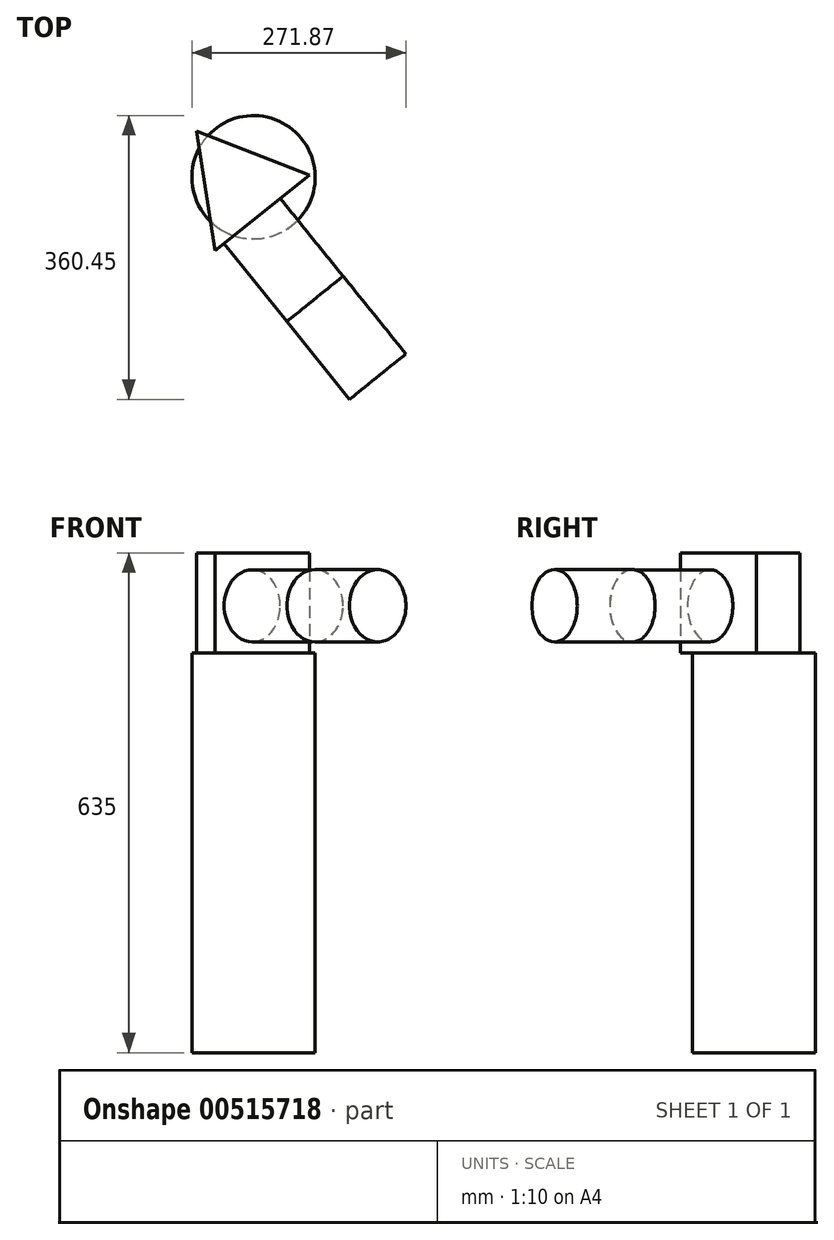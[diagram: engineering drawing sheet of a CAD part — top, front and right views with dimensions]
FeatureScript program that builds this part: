
annotation { "Feature Type Name" : "Feature", "Feature Type Description" : "" }
export const myFeature = defineFeature(function(context is Context, id is Id, definition is map)
    precondition{}
    {
        {
            var Q0;
            Q0=qCreatedBy(makeId("Top.planeOp"),FACE);
            var sketch = newSketch(context, id + "F0", { "sketchPlane" : qUnion([Q0])});
            skCircle(sketch, "E0", {"center": v(-8.38, -11.93) * mm, "radius": 78.33 * mm});
            skSolve(sketch);
        }
        {
            var Q0;
            Q0 = qSketchRegion(id + "F0", true);
            extrude(context, id + "F1", {"entities" : qUnion([Q0]), "depth" : 508 * mm, "offsetDistance" : 25.4 * mm});
        }
        {
            var Q0;
            Q0=makeQuery(id+"F1.opExtrude","CAP_FACE",FACE,{"disambiguationData":[OSD([sQuery(id+"F0.wireOp",EDGE,"E0")])],"isStart":false});
            var sketch = newSketch(context, id + "F2", { "sketchPlane" : qUnion([Q0])});
            skCircle(sketch, "E1.cCircle", {"center": v(-25.04, -22.65) * mm, "radius": 44.32 * mm, "construction": true});
            skLineSegment(sketch, "E1.0", {"start": v(62.53, -8.96) * mm, "end": v(-56.98, -105.34) * mm});
            skLineSegment(sketch, "E1.1", {"start": v(-56.98, -105.34) * mm, "end": v(-80.7, 46.35) * mm});
            skLineSegment(sketch, "E1.2", {"start": v(-80.7, 46.35) * mm, "end": v(62.53, -8.96) * mm});
            skPoint(sketch, "E1.0.midPoint", {"position": v(2.78, -57.15) * mm});
            skSolve(sketch);
        }
        {
            var Q0;
            Q0 = qSketchRegion(id + "F2", true);
            extrude(context, id + "F3", {"entities" : qUnion([Q0]), "operationType" : NewBodyOperationType.ADD, "depth" : 127 * mm, "offsetDistance" : 25.4 * mm});
        }
        {
            var Q0;
            Q0=makeQuery(id+"F3.opExtrude","SWEPT_FACE",FACE,{"disambiguationData":[OSD([sQuery(id+"F2.wireOp",EDGE,"E1.0")])]});
            var sketch = newSketch(context, id + "F4", { "sketchPlane" : qUnion([Q0])});
            skCircle(sketch, "E2", {"center": v(-50.2, 567.72) * mm, "radius": 45.7 * mm});
            skSolve(sketch);
        }
        {
            var Q0;
            Q0 = qSketchRegion(id + "F4", true);
            extrude(context, id + "F5", {"entities" : qUnion([Q0]), "operationType" : NewBodyOperationType.ADD, "depth" : 127 * mm, "offsetDistance" : 25.4 * mm});
        }
        {
            var Q0;
            Q0=makeQuery(id+"F5.opExtrude","CAP_FACE",FACE,{"disambiguationData":[OSD([sQuery(id+"F4.wireOp",EDGE,"E2")])],"isStart":false});
            var sketch = newSketch(context, id + "F6", { "sketchPlane" : qUnion([Q0])});
            skCircle(sketch, "E3", {"center": v(-50.2, 567.72) * mm, "radius": 45.94 * mm});
            skSolve(sketch);
        }
        {
            var Q0;
            Q0 = qSketchRegion(id + "F6", true);
            extrude(context, id + "F7", {"entities" : qUnion([Q0]), "operationType" : NewBodyOperationType.ADD, "depth" : 127 * mm, "offsetDistance" : 25.4 * mm});
        }
    });
